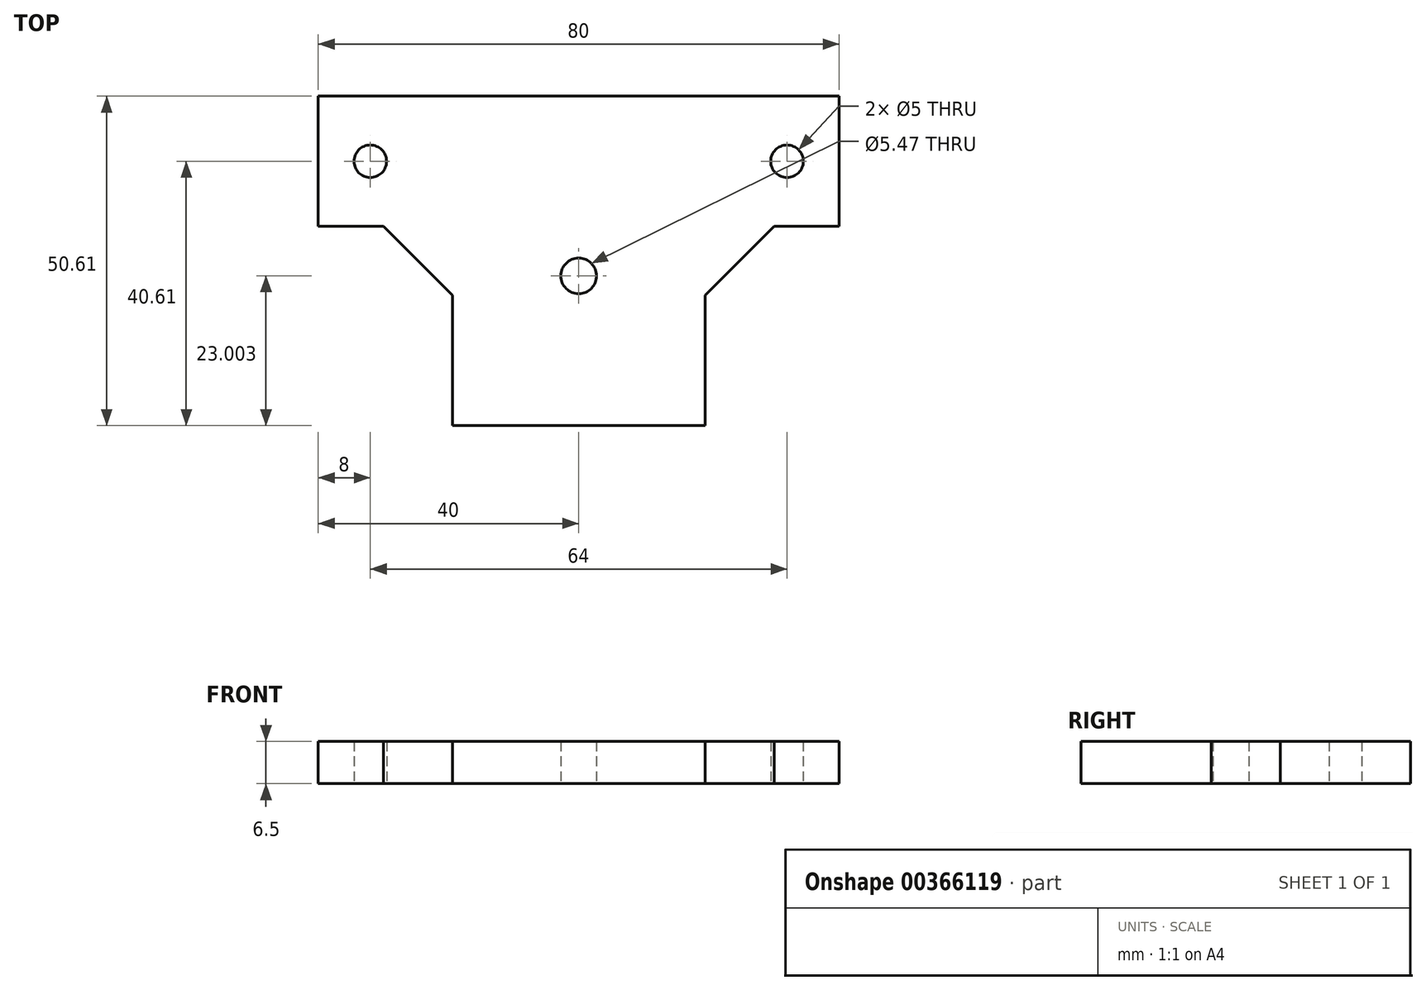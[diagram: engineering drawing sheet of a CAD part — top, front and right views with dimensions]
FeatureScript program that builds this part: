
annotation { "Feature Type Name" : "Feature", "Feature Type Description" : "" }
export const myFeature = defineFeature(function(context is Context, id is Id, definition is map)
    precondition{}
    {
        {
            var Q0;
            Q0=qCreatedBy(makeId("Top.planeOp"),FACE);
            var sketch = newSketch(context, id + "F0", { "sketchPlane" : qUnion([Q0])});
            skLineSegment(sketch, "E0", {"start": v(-40, 0) * mm, "end": v(40, 0) * mm});
            skLineSegment(sketch, "E1", {"start": v(-40, 0) * mm, "end": v(-40, -20) * mm});
            skLineSegment(sketch, "E2", {"start": v(-40, -20) * mm, "end": v(-30, -20) * mm});
            skLineSegment(sketch, "E3", {"start": v(-30, -20) * mm, "end": v(-19.4, -30.6) * mm});
            skLineSegment(sketch, "E4", {"start": v(-19.4, -30.6) * mm, "end": v(-19.4, -50.6) * mm});
            skLineSegment(sketch, "E5", {"start": v(-19.4, -50.6) * mm, "end": v(19.4, -50.6) * mm});
            skLineSegment(sketch, "E6.MirrorCS", {"start": v(40, 0) * mm, "end": v(40, -20) * mm});
            skLineSegment(sketch, "E7.MirrorCS", {"start": v(40, -20) * mm, "end": v(30, -20) * mm});
            skLineSegment(sketch, "E8.MirrorCS", {"start": v(30, -20) * mm, "end": v(19.4, -30.6) * mm});
            skLineSegment(sketch, "E9.MirrorCS", {"start": v(19.4, -30.6) * mm, "end": v(19.4, -50.6) * mm});
            skCircle(sketch, "E10", {"center": v(-32, -10) * mm, "radius": 2.5 * mm});
            skCircle(sketch, "E11", {"center": v(32, -10) * mm, "radius": 2.5 * mm});
            skCircle(sketch, "E12", {"center": v(0, -27.6) * mm, "radius": 2.74 * mm});
            skSolve(sketch);
        }
        {
            var Q0;
            Q0 = qSketchRegion(id + "F0", true);
            var Q1;
            Q1=makeQuery(id+"F0.imprint","IMPRINT",FACE,{"disambiguationData":[TD([[makeQuery(id+"F0.imprint","IMPRINT",EDGE,{"derivedFrom":sQuery(id+"F0.wireOp",EDGE,"E0")}),-1.0]])]});
            extrude(context, id + "F1", {"entities" : qUnion([Q0, Q1]), "depth" : 6.5 * mm});
        }
    });
